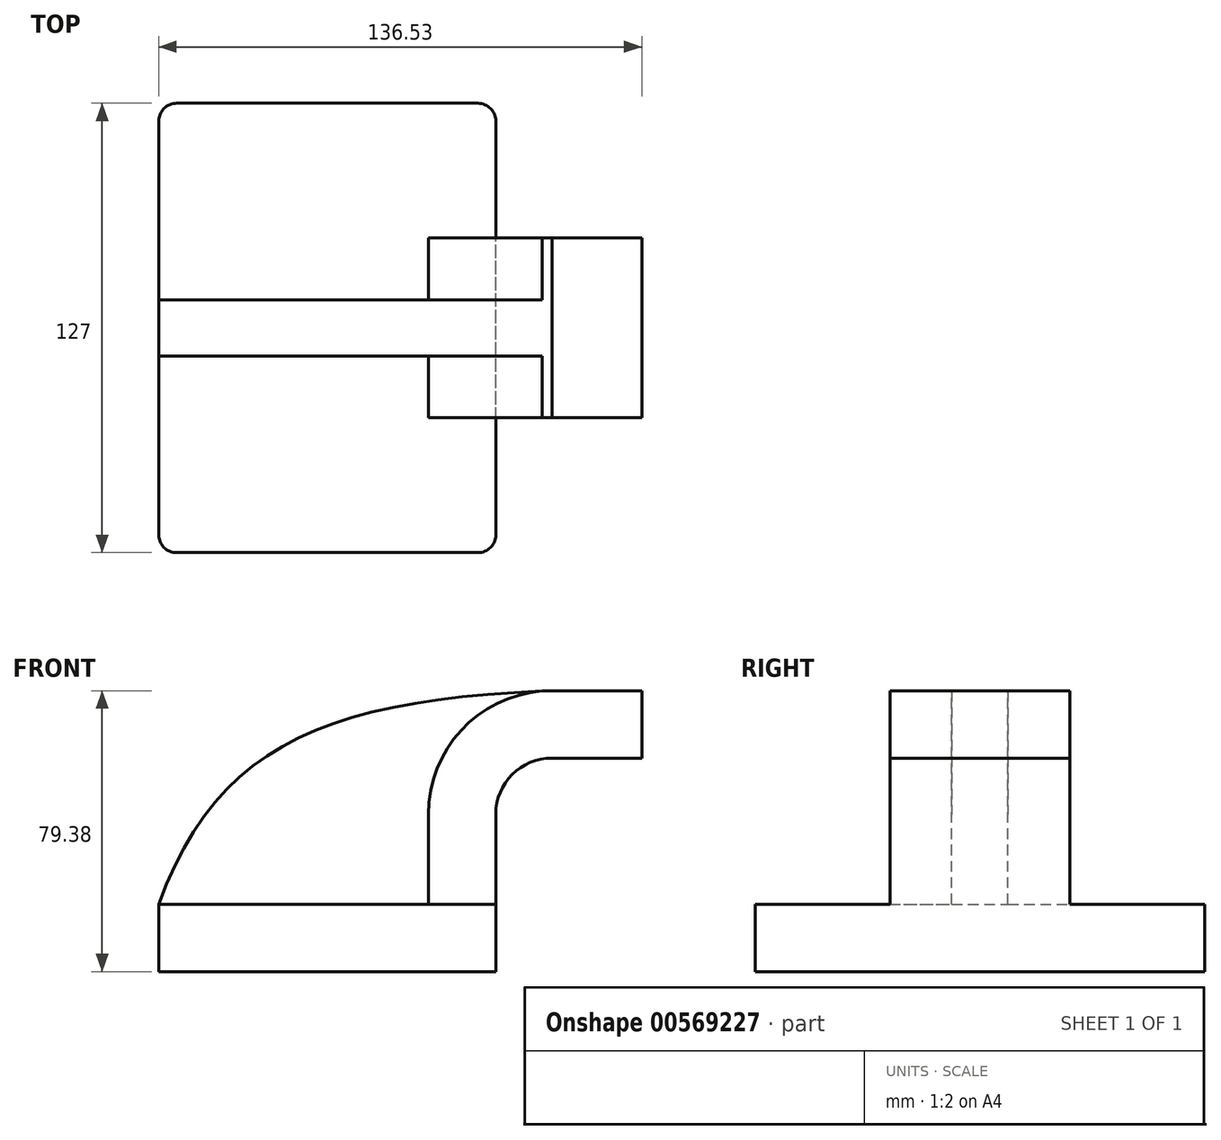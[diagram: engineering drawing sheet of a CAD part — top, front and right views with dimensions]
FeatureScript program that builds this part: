
annotation { "Feature Type Name" : "Feature", "Feature Type Description" : "" }
export const myFeature = defineFeature(function(context is Context, id is Id, definition is map)
    precondition{}
    {
        {
            var Q0;
            Q0=qCreatedBy(makeId("Front.planeOp"),FACE);
            var sketch = newSketch(context, id + "F0", { "sketchPlane" : qUnion([Q0])});
            skLineSegment(sketch, "E0.bottom", {"start": v(-47.63, 9.52) * mm, "end": v(47.63, 9.53) * mm});
            skLineSegment(sketch, "E0.top", {"start": v(-47.63, -9.53) * mm, "end": v(47.63, -9.53) * mm});
            skLineSegment(sketch, "E0.left", {"start": v(-47.63, 9.52) * mm, "end": v(-47.63, -9.53) * mm});
            skLineSegment(sketch, "E0.right", {"start": v(47.63, 9.53) * mm, "end": v(47.63, -9.52) * mm});
            skPoint(sketch, "E0.middle", {"position": v(0, 0) * mm});
            skLineSegment(sketch, "E1.bottom", {"start": v(88.9, 29.15) * mm, "end": v(139.7, 29.15) * mm});
            skLineSegment(sketch, "E1.top", {"start": v(88.9, 79.95) * mm, "end": v(139.7, 79.95) * mm});
            skLineSegment(sketch, "E1.left", {"start": v(88.9, 29.15) * mm, "end": v(88.9, 79.95) * mm});
            skLineSegment(sketch, "E1.right", {"start": v(139.7, 29.15) * mm, "end": v(139.7, 79.95) * mm});
            skPoint(sketch, "E1.middle", {"position": v(114.3, 54.55) * mm});
            skLineSegment(sketch, "E2", {"start": v(47.62, 9.53) * mm, "end": v(47.62, 34.93) * mm});
            skArc(sketch, "E3", {"start": v(47.62, 34.93) * mm, "mid": v(52.27, 46.15) * mm, "end": v(63.5, 50.8) * mm});
            skLineSegment(sketch, "E4", {"start": v(63.5, 50.8) * mm, "end": v(88.9, 50.8) * mm});
            skLineSegment(sketch, "E5.0", {"start": v(63.5, 69.85) * mm, "end": v(88.9, 69.85) * mm});
            skArc(sketch, "E5.1", {"start": v(28.57, 34.93) * mm, "mid": v(38.8, 59.62) * mm, "end": v(63.5, 69.85) * mm});
            skLineSegment(sketch, "E5.2", {"start": v(28.57, 9.53) * mm, "end": v(28.57, 34.93) * mm});
            skFitSpline(sketch, "E6", {"points": [v(-47.63, 9.52) * mm, v(63.5, 69.85) * mm], "startDerivative": vector(49.4, 135.15) * mm, "endDerivative": vector(190.5, 7.15) * mm});
            skSolve(sketch);
        }
        {
            var Q0;
            Q0=makeQuery(id+"F0.imprint","IMPRINT",FACE,{"disambiguationData":[TD([[makeQuery(id+"F0.imprint","IMPRINT",EDGE,{"derivedFrom":sQuery(id+"F0.wireOp",EDGE,"E0.top")}),1.0]])]});
            extrude(context, id + "F1", {"entities" : qUnion([Q0]), "endBound" : BoundingType.SYMMETRIC, "depth" : 127 * mm, "offsetDistance" : 25.4 * mm});
        }
        {
            var Q0;
            {var subQ0=sQuery(id+"F0.wireOp",EDGE,"E2");Q0=makeQuery(id+"F0.imprint","IMPRINT",FACE,{"disambiguationData":[TD([[makeQuery(id+"F0.imprint","IMPRINT",EDGE,{"derivedFrom":subQ0}),1.0]])]});}
            extrude(context, id + "F2", {"entities" : qUnion([Q0]), "operationType" : NewBodyOperationType.ADD, "endBound" : BoundingType.SYMMETRIC, "depth" : 50.8 * mm, "offsetDistance" : 25.4 * mm});
        }
        {
            var Q0;
            {var subQ3=sQuery(id+"F0.wireOp",EDGE,"E5.2");Q0=makeQuery(id+"F0.imprint","IMPRINT",FACE,{"disambiguationData":[TD([[makeQuery(id+"F0.imprint","IMPRINT",EDGE,{"derivedFrom":subQ3}),1.0]])]});}
            extrude(context, id + "F3", {"entities" : qUnion([Q0]), "operationType" : NewBodyOperationType.ADD, "endBound" : BoundingType.SYMMETRIC, "depth" : 15.88 * mm, "offsetDistance" : 25.4 * mm});
        }
        {
            var Q0;
            Q0=makeQuery(id+"F1.opExtrude","CAP_EDGE",EDGE,{"disambiguationData":[OSD([sQuery(id+"F0.wireOp",EDGE,"E0.left")])],"isStart":false});
            var Q1;
            Q1=makeQuery(id+"F1.opExtrude","CAP_EDGE",EDGE,{"disambiguationData":[OSD([sQuery(id+"F0.wireOp",EDGE,"E0.right")])],"isStart":false});
            var Q2;
            Q2=makeQuery(id+"F1.opExtrude","CAP_EDGE",EDGE,{"disambiguationData":[OSD([sQuery(id+"F0.wireOp",EDGE,"E0.left")])],"isStart":true});
            var Q3;
            Q3=makeQuery(id+"F1.opExtrude","CAP_EDGE",EDGE,{"disambiguationData":[OSD([sQuery(id+"F0.wireOp",EDGE,"E0.right")])],"isStart":true});
            fillet(context, id + "F4", {"entities" : qUnion([Q0, Q1, Q2, Q3]), "radius" : 5.08 * mm, "tangentPropagation" : true, "allowEdgeOverflow" : false});
        }
    });
